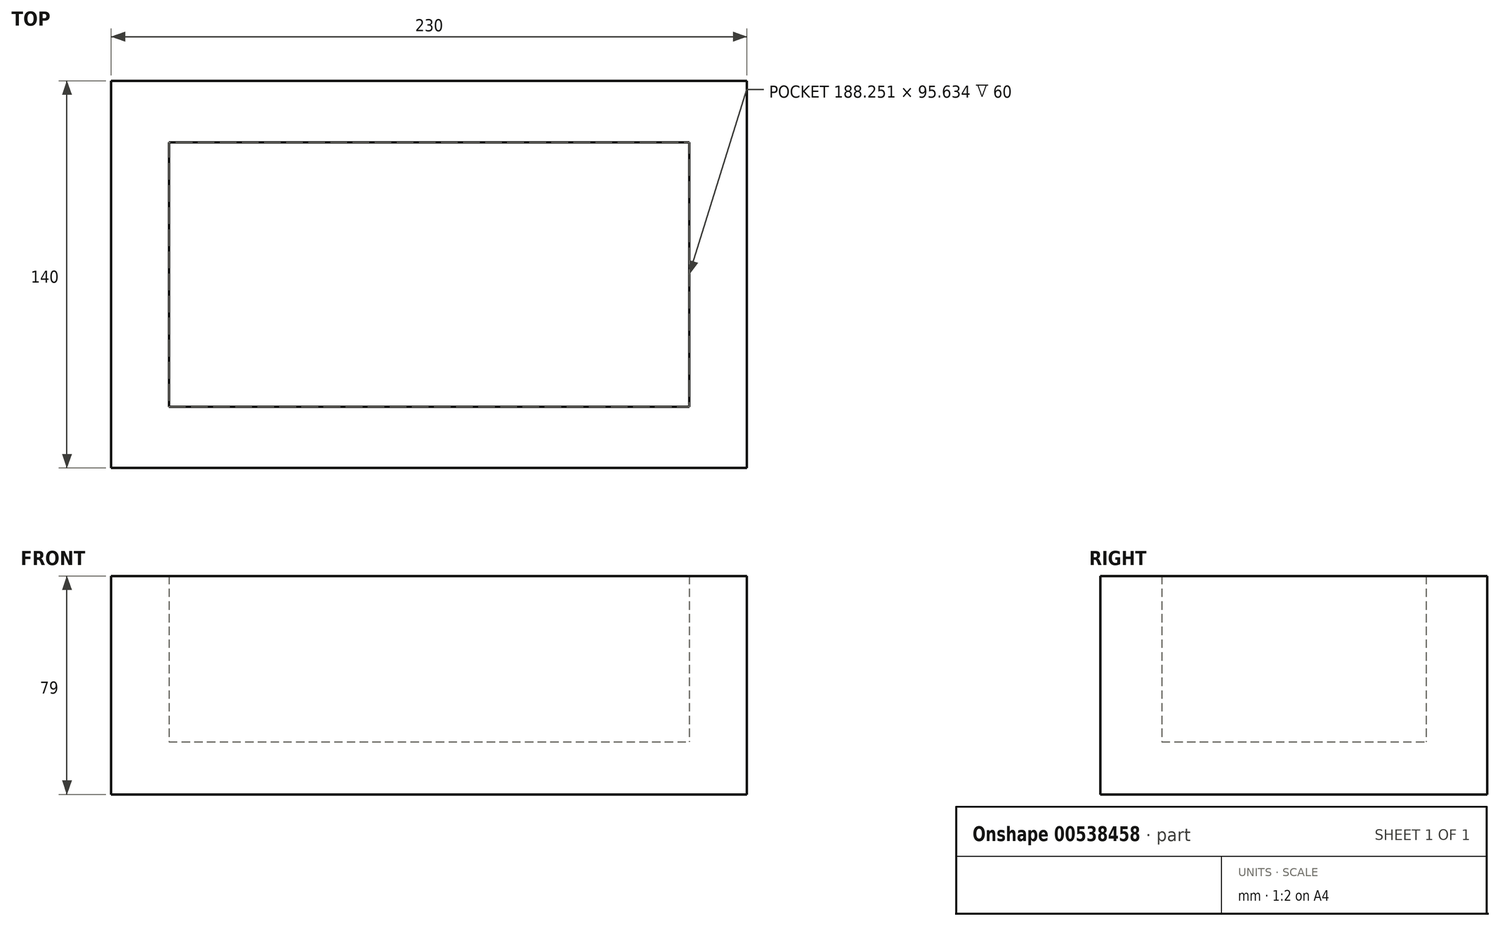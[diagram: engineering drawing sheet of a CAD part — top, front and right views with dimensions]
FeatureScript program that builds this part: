
annotation { "Feature Type Name" : "Feature", "Feature Type Description" : "" }
export const myFeature = defineFeature(function(context is Context, id is Id, definition is map)
    precondition{}
    {
        {
            var Q0;
            Q0=qCreatedBy(makeId("Top.planeOp"),FACE);
            var sketch = newSketch(context, id + "F0", { "sketchPlane" : qUnion([Q0])});
            skLineSegment(sketch, "E0.bottom", {"start": v(115, -70) * mm, "end": v(-115, -70) * mm});
            skLineSegment(sketch, "E0.top", {"start": v(115, 70) * mm, "end": v(-115, 70) * mm});
            skLineSegment(sketch, "E0.left", {"start": v(115, -70) * mm, "end": v(115, 70) * mm});
            skLineSegment(sketch, "E0.right", {"start": v(-115, -70) * mm, "end": v(-115, 70) * mm});
            skPoint(sketch, "E0.middle", {"position": v(0, 0) * mm});
            skSolve(sketch);
        }
        {
            var Q0;
            Q0=qSketchRegion(id+"F0",true);
            extrude(context, id + "F1", {"entities" : qUnion([Q0]), "depth" : 19 * mm, "offsetDistance" : 25 * mm});
        }
        {
            var Q0;
            Q0=makeQuery(id+"F1.opExtrude","CAP_FACE",FACE,{"disambiguationData":[OSD([sQuery(id+"F0.wireOp",EDGE,"E0.bottom"),sQuery(id+"F0.wireOp",EDGE,"E0.top"),sQuery(id+"F0.wireOp",EDGE,"E0.left"),sQuery(id+"F0.wireOp",EDGE,"E0.right")])],"isStart":false});
            var sketch = newSketch(context, id + "F2", { "sketchPlane" : qUnion([Q0])});
            skLineSegment(sketch, "E1.bottom", {"start": v(-94.13, -47.82) * mm, "end": v(94.13, -47.82) * mm});
            skLineSegment(sketch, "E1.top", {"start": v(-94.13, 47.82) * mm, "end": v(94.13, 47.82) * mm});
            skLineSegment(sketch, "E1.left", {"start": v(-94.13, -47.82) * mm, "end": v(-94.13, 47.82) * mm});
            skLineSegment(sketch, "E1.right", {"start": v(94.13, -47.82) * mm, "end": v(94.13, 47.82) * mm});
            skPoint(sketch, "E1.middle", {"position": v(0, 0) * mm});
            skSolve(sketch);
        }
        {
            var Q0;
            Q0=makeQuery(id+"F2.imprint","IMPRINT",FACE,{"disambiguationData":[TD([[makeQuery(id+"F2.imprint","IMPRINT",EDGE,{"derivedFrom":sQuery(id+"F2.wireOp",EDGE,"E1.bottom")}),-1.0]])]});
            extrude(context, id + "F3", {"entities" : qUnion([Q0]), "operationType" : NewBodyOperationType.ADD, "depth" : 60 * mm, "offsetDistance" : 25 * mm});
        }
    });
